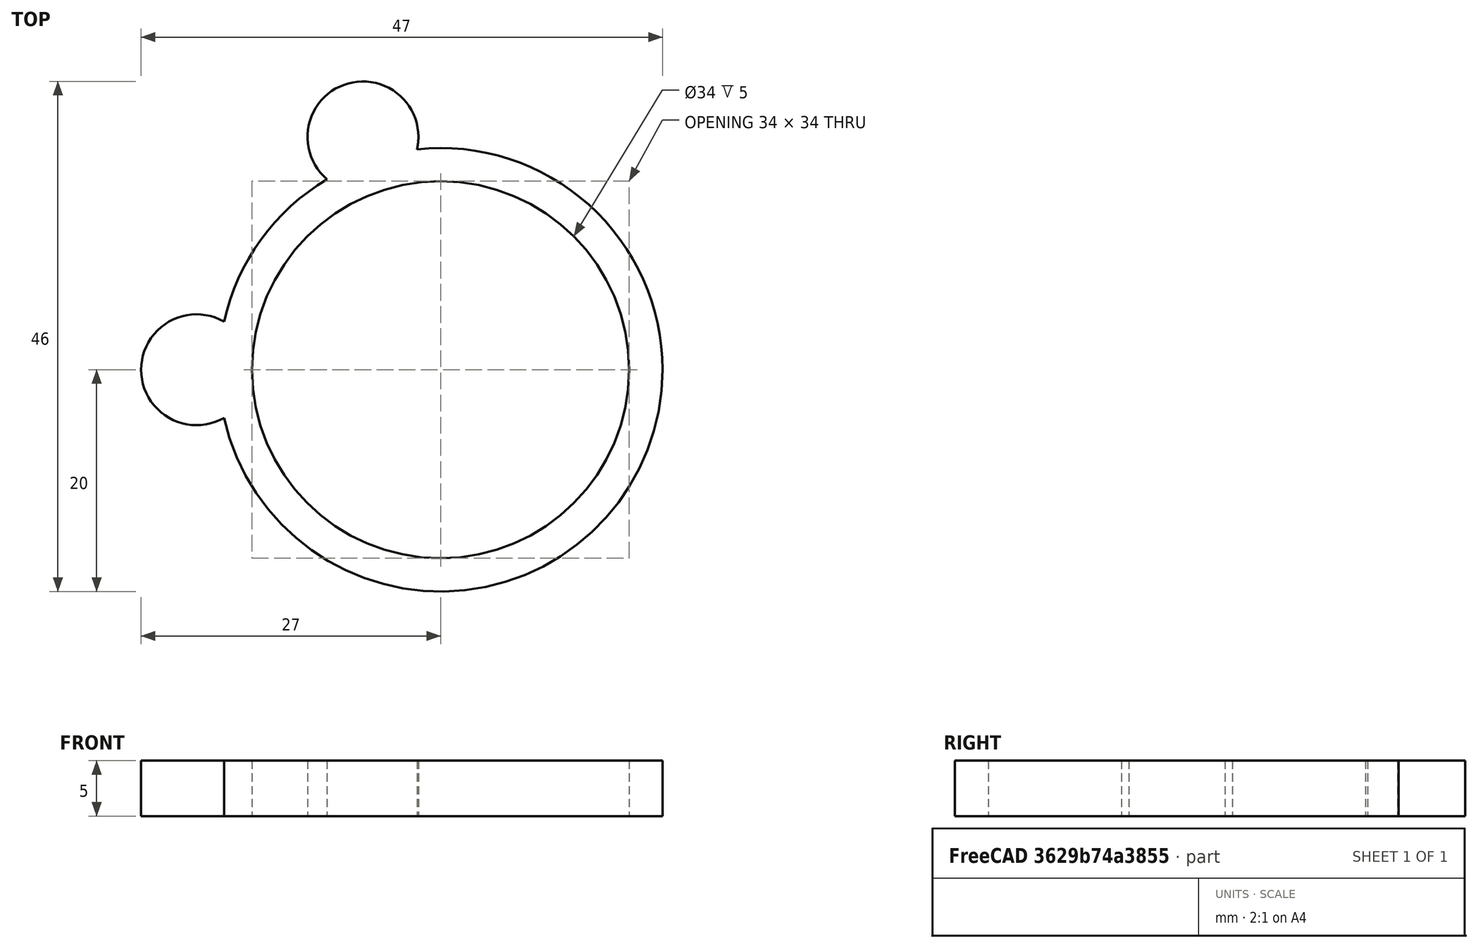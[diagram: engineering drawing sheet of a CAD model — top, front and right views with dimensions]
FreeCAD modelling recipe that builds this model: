
FCSTD DOCUMENT  (FreeCAD 0.20R29410 (Git))
Label: oso
License: Creative Commons Attribution
LicenseURL: http://creativecommons.org/licenses/by/4.0/
objects: Part::Cylinder×4, Part::Cut×1, Part::Fuse×1, Part::MultiFuse×1
note: 7 computed .brp shape members not serialized (recipe doc carries the construction recipe); baked Part::Feature solids carry a one-line shape summary decoded from their .brp

FEATURE [Part::Cylinder] Cylinder  label="Cilindro"
  Angle = 360
  AttacherType = Attacher::AttachEngine3D
  FirstAngle = 0
  Height = 5
  Radius = 20
  SecondAngle = 0
FEATURE [Part::Cylinder] Cylinder001  label="Cilindro001"
  Angle = 360
  AttacherType = Attacher::AttachEngine3D
  FirstAngle = 0
  Height = 5
  Radius = 17
  SecondAngle = 0
FEATURE [Part::Cut] Cut
  Base = -> Cylinder
  Refine = true
  Tool = -> Cylinder001
FEATURE [Part::Cylinder] Cylinder002  label="Cilindro002"
  Angle = 360
  AttacherType = Attacher::AttachEngine3D
  FirstAngle = 0
  Height = 5
  Placement = pos=(-22,0,0) rot=(0,0,1;0rad)
  Radius = 5
  SecondAngle = 0
FEATURE [Part::Cylinder] Cylinder003  label="Cilindro003"
  Angle = 360
  AttacherType = Attacher::AttachEngine3D
  FirstAngle = 0
  Height = 5
  Placement = pos=(-7,21,0) rot=(0,0,1;0rad)
  Radius = 5
  SecondAngle = 0
FEATURE [Part::Fuse] Fusion
  Base = -> Cut
  Refine = true
  Tool = -> Cylinder002
FEATURE [Part::MultiFuse] Fusion001
  Refine = true
  Shapes = -> [Fusion,Cylinder003]
